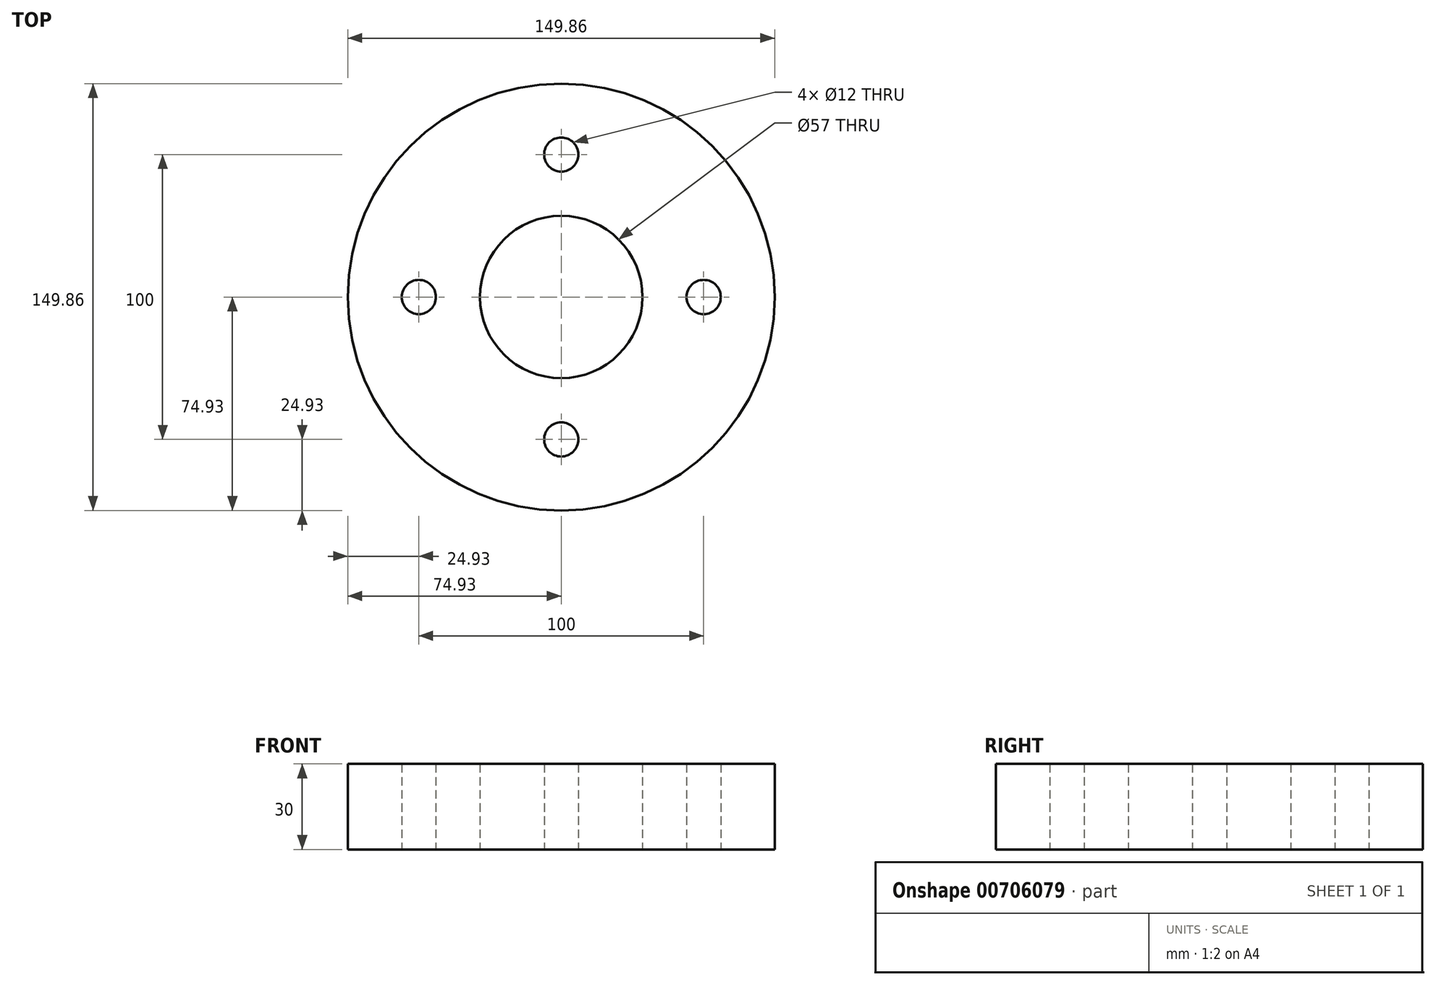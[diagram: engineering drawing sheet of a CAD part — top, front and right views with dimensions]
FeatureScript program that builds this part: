
annotation { "Feature Type Name" : "Feature", "Feature Type Description" : "" }
export const myFeature = defineFeature(function(context is Context, id is Id, definition is map)
    precondition{}
    {
        {
            var Q0;
            Q0=qCreatedBy(makeId("Top.planeOp"),FACE);
            var sketch = newSketch(context, id + "F0", { "sketchPlane" : qUnion([Q0])});
            skCircle(sketch, "E0", {"center": v(0, 0) * mm, "radius": 74.93 * mm});
            skCircle(sketch, "E1", {"center": v(0, 0) * mm, "radius": 28.5 * mm});
            skCircle(sketch, "E2", {"center": v(0, 0) * mm, "radius": 50 * mm});
            skCircle(sketch, "E3", {"center": v(0, 50) * mm, "radius": 6 * mm});
            skCircle(sketch, "E4.1.0", {"center": v(-50, 0) * mm, "radius": 6 * mm});
            skCircle(sketch, "E4.2.0", {"center": v(0, -50) * mm, "radius": 6 * mm});
            skCircle(sketch, "E4.3.0", {"center": v(50, 0) * mm, "radius": 6 * mm});
            skSolve(sketch);
        }
        {
            var Q0;
            Q0=makeQuery(id+"F0.imprint","IMPRINT",FACE,{"disambiguationData":[TD([[makeQuery(id+"F0.imprint","IMPRINT",EDGE,{"derivedFrom":sQuery(id+"F0.wireOp",EDGE,"E0")}),1.0]])]});
            var Q1;
            Q1=makeQuery(id+"F0.imprint","IMPRINT",FACE,{"disambiguationData":[TD([[makeQuery(id+"F0.imprint","IMPRINT",EDGE,{"derivedFrom":sQuery(id+"F0.wireOp",EDGE,"E1")}),-1.0]])]});
            extrude(context, id + "F1", {"entities" : qUnion([Q0, Q1]), "depth" : 30 * mm, "offsetDistance" : 25.4 * mm});
        }
    });
